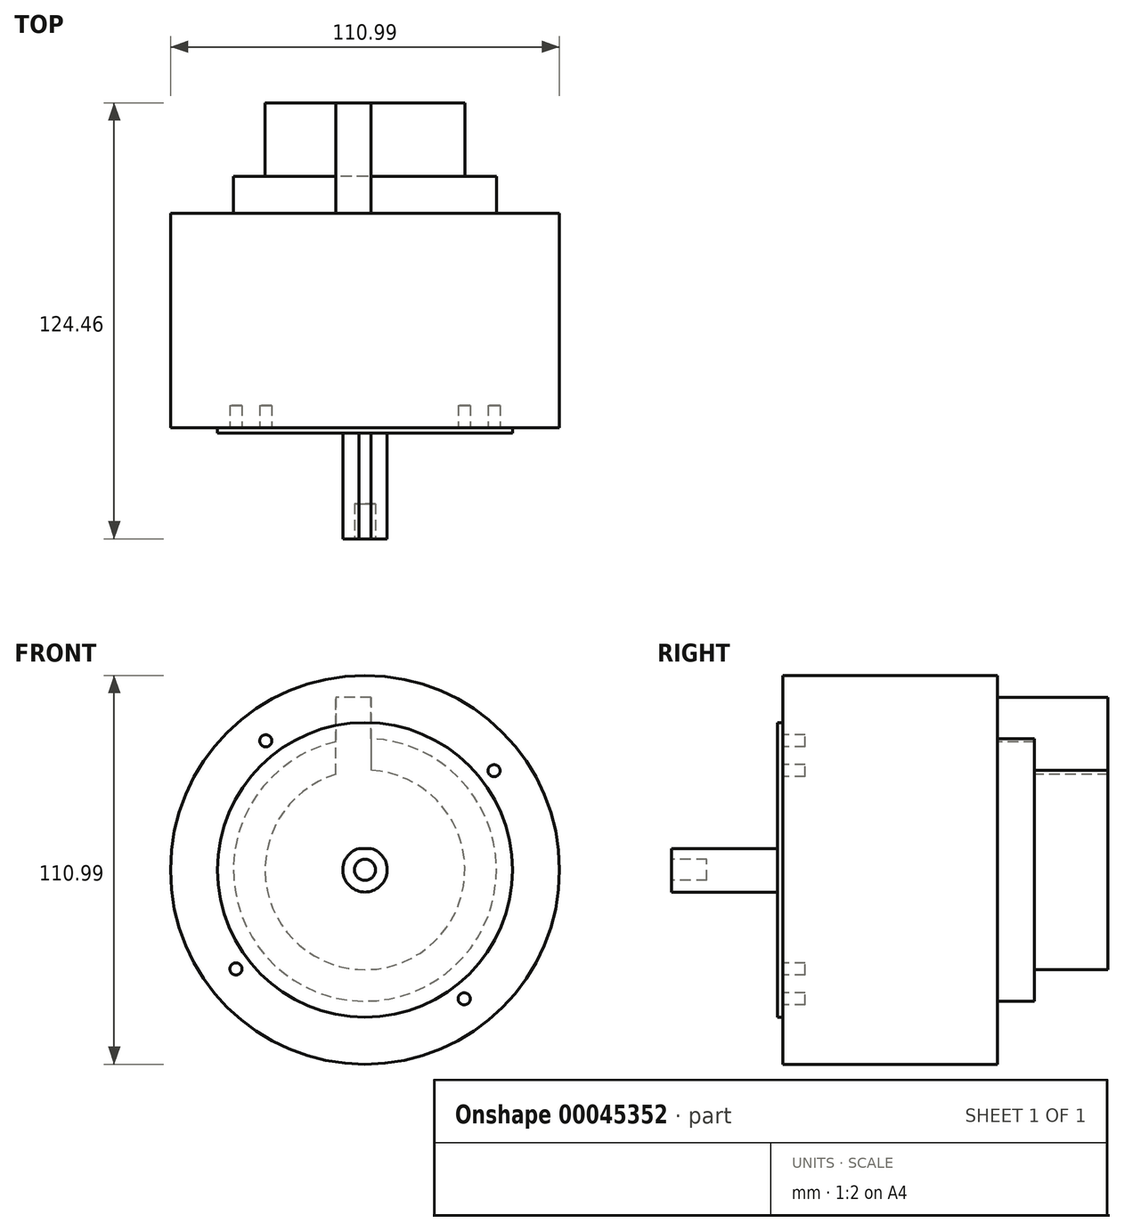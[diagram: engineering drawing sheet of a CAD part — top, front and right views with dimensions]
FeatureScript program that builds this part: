
annotation { "Feature Type Name" : "Feature", "Feature Type Description" : "" }
export const myFeature = defineFeature(function(context is Context, id is Id, definition is map)
    precondition{}
    {
        {
            var Q0;
            Q0=qCreatedBy(makeId("Front.planeOp"),FACE);
            var sketch = newSketch(context, id + "F0", { "sketchPlane" : qUnion([Q0])});
            skCircle(sketch, "E0", {"center": v(20.23, 17.59) * mm, "radius": 55.5 * mm});
            skSolve(sketch);
        }
        {
            var Q0;
            Q0 = qSketchRegion(id + "F0", true);
            extrude(context, id + "F1", {"entities" : qUnion([Q0]), "depth" : 61.1 * mm});
        }
        {
            var Q0;
            Q0=makeQuery(id+"F1.opExtrude","CAP_FACE",FACE,{"disambiguationData":[OSD([sQuery(id+"F0.wireOp",EDGE,"E0")])],"isStart":false});
            var sketch = newSketch(context, id + "F2", { "sketchPlane" : qUnion([Q0])});
            skCircle(sketch, "E1", {"center": v(20.23, 17.59) * mm, "radius": 42.05 * mm});
            skSolve(sketch);
        }
        {
            var Q0;
            Q0 = qSketchRegion(id + "F2", true);
            extrude(context, id + "F3", {"entities" : qUnion([Q0]), "operationType" : NewBodyOperationType.ADD, "depth" : 1.52 * mm});
        }
        {
            var Q0;
            Q0=makeQuery(id+"F3.opExtrude","CAP_FACE",FACE,{"disambiguationData":[OSD([sQuery(id+"F2.wireOp",EDGE,"E1")])],"isStart":false});
            var sketch = newSketch(context, id + "F4", { "sketchPlane" : qUnion([Q0])});
            skArc(sketch, "E2", {"start": v(18.45, 23.67) * mm, "mid": v(20.23, 11.25) * mm, "end": v(22, 23.67) * mm});
            skLineSegment(sketch, "E3.top", {"start": v(18.45, 23.67) * mm, "end": v(22, 23.67) * mm});
            skSolve(sketch);
        }
        {
            var Q0;
            Q0 = qSketchRegion(id + "F4", true);
            extrude(context, id + "F5", {"entities" : qUnion([Q0]), "operationType" : NewBodyOperationType.ADD, "depth" : 30.23 * mm, "hasSecondDirection" : true, "secondDirectionOppositeDirection" : true, "secondDirectionDepth" : 92.8 * mm});
        }
        {
            var Q0;
            Q0=makeQuery(id+"F1.opExtrude","CAP_FACE",FACE,{"disambiguationData":[OSD([sQuery(id+"F0.wireOp",EDGE,"E0")])],"isStart":true});
            var sketch = newSketch(context, id + "F6", { "sketchPlane" : qUnion([Q0])});
            skCircle(sketch, "E4", {"center": v(-20.23, 17.59) * mm, "radius": 37.5 * mm});
            skSolve(sketch);
        }
        {
            var Q0;
            Q0 = qSketchRegion(id + "F6", true);
            extrude(context, id + "F7", {"entities" : qUnion([Q0]), "operationType" : NewBodyOperationType.ADD, "depth" : 10.6 * mm});
        }
        {
            var Q0;
            Q0=makeQuery(id+"F7.opExtrude","CAP_FACE",FACE,{"disambiguationData":[OSD([sQuery(id+"F6.wireOp",EDGE,"E4")])],"isStart":false});
            var sketch = newSketch(context, id + "F8", { "sketchPlane" : qUnion([Q0])});
            skCircle(sketch, "E5", {"center": v(-20.23, 17.59) * mm, "radius": 28.5 * mm});
            skSolve(sketch);
        }
        {
            var Q0;
            Q0 = qSketchRegion(id + "F8", true);
            extrude(context, id + "F9", {"entities" : qUnion([Q0]), "operationType" : NewBodyOperationType.ADD, "depth" : 21 * mm});
        }
        {
            var Q0;
            Q0=makeQuery(id+"F1.opExtrude","CAP_FACE",FACE,{"disambiguationData":[OSD([sQuery(id+"F0.wireOp",EDGE,"E0")])],"isStart":false});
            var sketch = newSketch(context, id + "F10", { "sketchPlane" : qUnion([Q0])});
            skCircle(sketch, "E6", {"center": v(57.04, 45.88) * mm, "radius": 1.73 * mm});
            skCircle(sketch, "E7.1.0", {"center": v(-8.06, 54.4) * mm, "radius": 1.73 * mm});
            skCircle(sketch, "E7.2.0", {"center": v(-16.59, -10.7) * mm, "radius": 1.73 * mm});
            skCircle(sketch, "E7.3.0", {"center": v(48.52, -19.23) * mm, "radius": 1.73 * mm});
            skPoint(sketch, "E7.center", {"position": v(20.23, 17.59) * mm});
            skSolve(sketch);
        }
        {
            var Q0;
            Q0 = qSketchRegion(id + "F10", true);
            extrude(context, id + "F11", {"entities" : qUnion([Q0]), "operationType" : NewBodyOperationType.REMOVE, "oppositeDirection" : true, "depth" : 6.35 * mm});
        }
        {
            var Q0;
            Q0=makeQuery(id+"F9.opExtrude","CAP_FACE",FACE,{"disambiguationData":[OSD([sQuery(id+"F8.wireOp",EDGE,"E5")])],"isStart":false});
            var sketch = newSketch(context, id + "F12", { "sketchPlane" : qUnion([Q0])});
            skLineSegment(sketch, "E8", {"start": v(-11.94, 16.85) * mm, "end": v(-11.94, 66.85) * mm});
            skLineSegment(sketch, "E9", {"start": v(-11.94, 66.85) * mm, "end": v(-21.94, 66.85) * mm});
            skLineSegment(sketch, "E10", {"start": v(-21.94, 66.85) * mm, "end": v(-21.94, 16.85) * mm});
            skLineSegment(sketch, "E11", {"start": v(-21.94, 16.85) * mm, "end": v(-11.94, 16.85) * mm});
            skSolve(sketch);
        }
        {
            var Q0;
            Q0 = qSketchRegion(id + "F12", true);
            extrude(context, id + "F13", {"entities" : qUnion([Q0]), "operationType" : NewBodyOperationType.ADD, "oppositeDirection" : true, "depth" : 40 * mm});
        }
        {
            var Q0;
            Q0=makeQuery(id+"F5.opExtrude","CAP_FACE",FACE,{"disambiguationData":[OSD([sQuery(id+"F4.wireOp",EDGE,"E2"),sQuery(id+"F4.wireOp",EDGE,"E3.top")])],"isStart":false});
            var sketch = newSketch(context, id + "F14", { "sketchPlane" : qUnion([Q0])});
            skCircle(sketch, "E12", {"center": v(20.23, 17.59) * mm, "radius": 3 * mm});
            skSolve(sketch);
        }
        {
            var Q0;
            Q0 = qSketchRegion(id + "F14", true);
            extrude(context, id + "F15", {"entities" : qUnion([Q0]), "operationType" : NewBodyOperationType.REMOVE, "oppositeDirection" : true, "depth" : 10 * mm});
        }
    });
